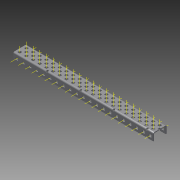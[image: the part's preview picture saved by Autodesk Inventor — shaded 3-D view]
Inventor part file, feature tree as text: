
AUTODESK INVENTOR PART (.ipt)
format: ipt  version: 2015 (Build 190159000, 159)  size: 2,108,928 bytes
history: native  units: in
note: dims shown in document units (in); Inventor stores cm internally (conversion verified against a paired STEP export)
features: other x111, pattern_linear x3, sheet_metal_op x1, extrude x1, imported_body x1, sketch x1
ambient origin geometry x8: Origin, YZ Plane, XZ Plane, XY Plane, X Axis, Y Axis, Z Axis, Center Point
bodies: Body1 (feature_tree)
feature tree (118):
  sheet_metal_op  "Fold1"
  other  "C-Channel"
  extrude  "length cut"  Depth=0.5in
  other  "top axis"
  other  "inner axis"
  other  "front axis"
  other  "back axis"
  pattern_linear  "top axes"  Spacing1=0.5in  [1 undecoded]
  pattern_linear  "inner axes"  Spacing1=0.5in  [1 undecoded]
  pattern_linear  "horiz axes"  Spacing1=-10.5in  [1 undecoded]
  other  "right plane"
  imported_body  "Base1"
  sketch  "Sketch1"  dims[d1=0.0in d4=0.5in d5=0.7874in d7=0.5in d10=0.5in d13=0.5in d14=-10.5in d15=0.0in d16=0.0in d17=0.0in d18=0.0in d19=0.0in]
  other  "Work Point1"
  other  "Work Point2"
  other  "Work Point3"
  other  "Work Point4"
  other  "Work Axis5"
  other  "Work Axis6"
  other  "Work Axis7"
  other  "Work Axis8"
  other  "Work Axis11"
  other  "Work Axis12"
  other  "Work Axis13"
  other  "Work Axis14"
  other  "Work Axis15"
  other  "Work Axis18"
  other  "Work Axis19"
  other  "Work Axis20"
  other  "Work Axis23"
  other  "Work Axis24"
  other  "Work Axis25"
  other  "Work Axis26"
  other  "Work Axis30"
  other  "Work Axis31"
  other  "Work Axis32"
  other  "Work Axis33"
  other  "left plane"
  other  "Work Axis37"
  other  "Work Axis38"
  other  "Work Axis39"
  other  "Work Axis40"
  other  "Work Axis41"
  other  "Work Axis42"
  other  "Work Axis43"
  other  "Work Axis44"
  other  "Work Axis45"
  other  "Work Axis46"
  other  "Work Axis47"
  other  "Work Axis48"
  other  "Work Axis49"
  other  "Work Axis50"
  other  "Work Axis51"
  other  "Work Axis52"
  other  "Work Axis57"
  other  "Work Axis58"
  other  "Work Axis59"
  other  "Work Axis60"
  other  "Work Axis61"
  other  "Work Axis62"
  other  "Work Axis63"
  other  "Work Axis64"
  other  "Work Axis65"
  other  "Work Axis66"
  other  "Work Axis67"
  other  "Work Axis68"
  other  "Work Axis69"
  other  "Work Axis70"
  other  "Work Axis71"
  other  "Work Axis72"
  other  "Work Axis77"
  other  "Work Axis78"
  other  "Work Axis79"
  other  "Work Axis80"
  other  "Work Axis81"
  other  "Work Axis82"
  other  "Work Axis83"
  other  "Work Axis84"
  other  "Work Axis85"
  other  "Work Axis86"
  other  "Work Axis87"
  other  "Work Axis88"
  other  "Work Axis89"
  other  "Work Axis90"
  other  "Work Axis91"
  other  "Work Axis92"
  other  "Work Axis97"
  other  "Work Axis98"
  other  "Work Axis99"
  other  "Work Axis100"
  other  "Work Axis101"
  other  "Work Axis102"
  other  "Work Axis103"
  other  "Work Axis104"
  other  "Work Axis105"
  other  "Work Axis106"
  other  "Work Axis107"
  other  "Work Axis108"
  other  "Work Axis109"
  other  "Work Axis110"
  other  "Work Axis111"
  other  "Work Axis112"
  other  "Work Axis117"
  other  "Work Axis118"
  other  "Work Axis119"
  other  "Work Axis120"
  other  "Work Axis121"
  other  "Work Axis122"
  other  "Work Axis123"
  other  "Work Axis124"
  other  "Work Axis125"
  other  "Work Axis126"
  other  "Work Axis127"
  other  "Work Axis128"
  other  "Work Axis129"
  other  "Work Axis130"
  other  "Work Axis131"
  other  "Work Axis132"
note: 3 required parameter values undecoded (feature->parameter linkage not recoverable at this tier; creation-order binding heuristic only, values carry confidence <= 0.55)
